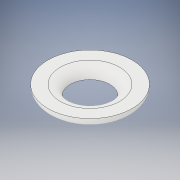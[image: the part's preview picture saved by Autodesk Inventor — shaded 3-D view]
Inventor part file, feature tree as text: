
AUTODESK INVENTOR PART (.ipt)
format: ipt  version: 2019 (Build 230136000, 136)  size: 146,944 bytes
history: native  units: mm
features: fillet x2, other x1, extrude x1, sketch x1
ambient origin geometry x8: Origin, YZ Plane, XZ Plane, XY Plane, X Axis, Y Axis, Z Axis, Center Point
bodies: Body1 (feature_tree)
feature tree (5):
  other  "Sólido1"
  extrude  "Extrusión1"  Depth=2.0mm
  fillet  "Empalme1"  Radius=2.0mm
  fillet  "Empalme2"  Radius=2.0mm
  sketch  "Boceto1"  dims[d0=8.0mm d1=17.0mm d2=2.0mm d3=0.0mm d4=2.0mm d5=2.0mm]
